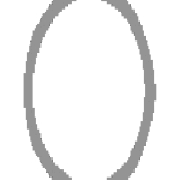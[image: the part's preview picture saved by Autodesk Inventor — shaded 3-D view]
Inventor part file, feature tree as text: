
AUTODESK INVENTOR PART (.ipt)
format: ipt  version: 2021 (Build 250183000, 183)  size: 109,568 bytes
history: native  units: in
note: dims shown in document units (in); Inventor stores cm internally (conversion verified against a paired STEP export)
features: other x4, sketch x3, plane x1
ambient origin geometry x8: Origin, YZ Plane, XZ Plane, XY Plane, X Axis, Y Axis, Z Axis, Center Point
bodies: Solid1 (feature_tree), Body (feature_tree)
feature tree (8):
  other  "Driven Length"
  other  "Frame Generator"
  other  "Start Plane"
  other  "End Plane"
  sketch  "Sketch"  dims[d2=20.5in d4=-0.0in d5=20.5in d6=0.12in d7=0.0in d8=90.0deg d9=20.5in]
  sketch  "Sketch2"  dims[d0=1.0in]
  plane  "Work Plane3"
  sketch  "Sketch3"  dims[d1=0.065in]
